# Revit family: FR_MEADRAIN_DM_Basic
name_source: partatom
category: Allgemeines Modell
revit_build: Autodesk Revit 2018 (Build: 20170223_1515(x64)
units: mm (PartAtom-declared; Revit-internal decimal feet)

## family parameters
Beim Laden mit Abzugskörper schneiden = Ja
Bemaßung runder Anschluss = Durchmesser verwenden
Gemeinsam genutzt = Nein
Kann Basisbauteil für Bewehrung sein = Nein
Raumberechnungspunkt = Nein
Teiletyp = Normal

## types (19) — shared parameters
B_Dimetre interieure_Manchon_SKUT = 150 mm  [stored 0.492126 ft]
Bauelement = Caniveau_ Eaux de surface
Beschreibung = System universel de drainage en béton polymère
Diametre exterieur du manchon_Avaloire = 122 mm  [stored 0.400262 ft]
Diametre exterieure manchon_SKUT = 160 mm  [stored 0.524934 ft]
Elément de drainage adapté pour = Les systèmes MEADRAIN DM répondent à toutes les exigences de construction de voies rapides et d'autoroutes.MEADRAIN DM est disponible en largeurs 100,150 et 200mm
Fiche technique produit = https://www.mea-group.com
Grille = Grille en fonte
Hersteller = MEA Bautechnik GmbH business unit MEA Water Management
Hersteller und Typ- Ausschreibender gleichwertig = comme MEA Bautechnik GmbH, modèle MEADRAIN DM
IfcDescription = System universel de drainage en béton polymère
IfcExportAs = IfcWasteTerminalType
IfcExportType = USERDEFINED
Lien pour les produit = https://www.mea-group.com
MEA Consignes de pose = y compris les fondations et l'enrobage
Materiaux lit/ fondations = conformément aux dessins et à la description du produits
Materiaux élément de drainage = Caniveau de drainage
Modell = MEADRAIN DM
Stirnplatte_Epaisseure = 3 mm  [stored 0.00984252 ft]
Techniques d'installation = Typ M
Typ element de drainage = Beton
Typenkommentare = Les systèmes MEADRAIN DM répondent à toutes les exigences de construction de voies rapides et d'autoroutes.MEADRAIN DM est disponible en largeurs 100,150 et 200mm
guid = cf6c1bd8-9bf4-4563-8c57-07955e2378ac
type de pente/ pourcentage de pente élement de drainage = sans pente

## per-type parameters (varying)
| type | B_Diametre interieure_Manchon_Element de revision | B_H01 | B_Hauteur_Avaloire | B_Largeur_Caniveau | Classe de charge element de drainage | Def Classe de charge_Caniveau | Diemetre exterieure manchon_Element de revision | Documents de mise en œuvre | Hauteur_Caniveau | Largeur nominal | Largeur_Caniveau | Largeur_Fondation | Longeur_Manchon_Avaloire | Longeur_Manchon_element de revision | MEA- largeur nominal | Numéro d'article_Avaloir | Numéro d'article_Caniveau | Numéro d'article_Element de revision | Numéro d'article_Grille 1 | Numéro d'article_Grille 2 | Numéro d'article_Manchon_element de revision | Numéro d'article_Plaque frontale | Numéro d'article_SKOT |
| DM 1010 | 2 mm  [stored 0.00656168 ft] | 265 mm  [stored 0.869423 ft] | 580 mm  [stored 1.90289 ft] | 154 mm  [stored 0.505249 ft] | F900 | F900 | 22 mm  [stored 0.0721785 ft] |  | 265 mm  [stored 0.869423 ft] | 100 mm  [stored 0.328084 ft] | 154 mm  [stored 0.505249 ft] | 250 mm  [stored 0.82021 ft] | 30 mm  [stored 0.0984252 ft] | 130 mm  [stored 0.426509 ft] | 1010 | 010712898 | 010712884 | 010712896 | - | 010153094 | - | 010712900 |  |
| DM 1500 | 2 mm  [stored 0.00656168 ft] | 280 mm  [stored 0.918635 ft] | 860 mm | 204 mm  [stored 0.669291 ft] | F900 | F900 | 22 mm  [stored 0.0721785 ft] |  | 280 mm  [stored 0.918635 ft] | 150 mm  [stored 0.492126 ft] | 204 mm  [stored 0.669291 ft] | 250 mm  [stored 0.82021 ft] | 194 mm  [stored 0.636483 ft] | 130 mm  [stored 0.426509 ft] | 1500 |  | 010712938 | 010712950 | 010151173 | 010151169 | - | 010712954 | 010712952 |
| DM 1540 | 140 mm  [stored 0.459318 ft] | 480 mm  [stored 1.5748 ft] | 860 mm | 204 mm  [stored 0.669291 ft] | F900 | F900 | 160 mm  [stored 0.524934 ft] |  | 480 mm  [stored 1.5748 ft] | 150 mm  [stored 0.492126 ft] | 204 mm  [stored 0.669291 ft] | 250 mm  [stored 0.82021 ft] | 194 mm  [stored 0.636483 ft] | 130 mm  [stored 0.426509 ft] | 1540 |  | 010712902 | 010712383 | 010151173 | 010151169 | 010712384 | 010712918 | 010712916 |
| DM 2000 | 180 mm  [stored 0.590551 ft] | 320 mm  [stored 1.04987 ft] | 700 mm  [stored 2.29659 ft] | 254 mm | F900 | F900 | 200 mm  [stored 0.656168 ft] |  | 320 mm  [stored 1.04987 ft] | 200 mm  [stored 0.656168 ft] | 254 mm | 250 mm  [stored 0.82021 ft] | 194 mm  [stored 0.636483 ft] | 180 mm  [stored 0.590551 ft] | 2000 |  | 010712357 | 010712386 | 010154236 | 010154237 | 010714908 | 010712375 | 010712369 |
| DM 2020 | 180 mm  [stored 0.590551 ft] | 420 mm  [stored 1.37795 ft] | 800 mm  [stored 2.62467 ft] | 254 mm | E600 | E600 | 200 mm  [stored 0.656168 ft] |  | 420 mm  [stored 1.37795 ft] | 200 mm  [stored 0.656168 ft] | 254 mm | 200 mm  [stored 0.656168 ft] | 194 mm  [stored 0.636483 ft] | 180 mm  [stored 0.590551 ft] | 2020 |  | 010712804 | 010712385 | 010154236 | 010154237 | 010714910 | 010712822 | 010712816 |
| DM 2040 | 180 mm  [stored 0.590551 ft] | 520 mm  [stored 1.70604 ft] | 950 mm  [stored 3.1168 ft] | 254 mm | E600 | E600 | 200 mm  [stored 0.656168 ft] | https://www.mea-group.com | 520 mm  [stored 1.70604 ft] | 200 mm  [stored 0.656168 ft] | 254 mm | 200 mm  [stored 0.656168 ft] | 194 mm  [stored 0.636483 ft] | 180 mm  [stored 0.590551 ft] | 2040 |  | 010712782 | 010712389 | 010154236 | 010154237 | 010714912 | 010712800 | 010712798 |
| DM 2050 | 180 mm  [stored 0.590551 ft] | 559 mm  [stored 1.83399 ft] | 950 mm  [stored 3.1168 ft] | 254 mm | E600 | E600 | 200 mm  [stored 0.656168 ft] |  | 559 mm  [stored 1.83399 ft] | 200 mm  [stored 0.656168 ft] | 254 mm | 200 mm  [stored 0.656168 ft] | 194 mm  [stored 0.636483 ft] | 180 mm  [stored 0.590551 ft] | 2050 |  | 010712762 | 010712390 | 010154236 | 010154237 | 010714914 | 010712780 | 010712778 |
| DM 1010 DAR | 2 mm  [stored 0.00656168 ft] | 265 mm  [stored 0.869423 ft] | 580 mm  [stored 1.90289 ft] | 154 mm  [stored 0.505249 ft] | F900 | F900 | 22 mm  [stored 0.0721785 ft] |  | 265 mm  [stored 0.869423 ft] | 100 mm  [stored 0.328084 ft] | 154 mm  [stored 0.505249 ft] | 250 mm  [stored 0.82021 ft] | 30 mm  [stored 0.0984252 ft] | 130 mm  [stored 0.426509 ft] | 1010 DAR | 010712892 | 010712884 | 010712896 | - | 010153094 | - | 010712900 |  |
| DM 1010 DAL | 2 mm  [stored 0.00656168 ft] | 265 mm  [stored 0.869423 ft] | 580 mm  [stored 1.90289 ft] | 154 mm  [stored 0.505249 ft] | F900 | F900 | 22 mm  [stored 0.0721785 ft] |  | 265 mm  [stored 0.869423 ft] | 100 mm  [stored 0.328084 ft] | 154 mm  [stored 0.505249 ft] | 250 mm  [stored 0.82021 ft] | 30 mm  [stored 0.0984252 ft] | 130 mm  [stored 0.426509 ft] | 1010 DAL | 010712888 | 010712884 | 010712896 | - | 010153094 | - | 010712900 |  |
| DM 1500 DAR | 2 mm  [stored 0.00656168 ft] | 280 mm  [stored 0.918635 ft] | 860 mm | 204 mm  [stored 0.669291 ft] | F900 | F900 | 22 mm  [stored 0.0721785 ft] |  | 280 mm  [stored 0.918635 ft] | 150 mm  [stored 0.492126 ft] | 204 mm  [stored 0.669291 ft] | 250 mm  [stored 0.82021 ft] | 194 mm  [stored 0.636483 ft] | 130 mm  [stored 0.426509 ft] | 1500 DAR |  | 010712956 | 010712950 | 010151173 | 010151169 | - | 010712954 | 010712952 |
| DM 1500 DAL | 2 mm  [stored 0.00656168 ft] | 280 mm  [stored 0.918635 ft] | 860 mm | 204 mm  [stored 0.669291 ft] | F900 | F900 | 22 mm  [stored 0.0721785 ft] |  | 280 mm  [stored 0.918635 ft] | 150 mm  [stored 0.492126 ft] | 204 mm  [stored 0.669291 ft] | 250 mm  [stored 0.82021 ft] | 194 mm  [stored 0.636483 ft] | 130 mm  [stored 0.426509 ft] | 1500 DAL |  | 010712938 | 010712950 | 010151173 | 010151169 | - | 010712954 | 010712952 |
| DM 1540 DAR | 140 mm  [stored 0.459318 ft] | 480 mm  [stored 1.5748 ft] | 860 mm | 204 mm  [stored 0.669291 ft] | F900 | F900 | 160 mm  [stored 0.524934 ft] |  | 480 mm  [stored 1.5748 ft] | 150 mm  [stored 0.492126 ft] | 204 mm  [stored 0.669291 ft] | 250 mm  [stored 0.82021 ft] | 194 mm  [stored 0.636483 ft] | 130 mm  [stored 0.426509 ft] | 1540 DAR |  | 010712910 | 010712383 | 010151173 | 010151169 | 010712384 | 010712918 | 010712916 |
| DM 1540 DAL | 140 mm  [stored 0.459318 ft] | 480 mm  [stored 1.5748 ft] | 860 mm | 204 mm  [stored 0.669291 ft] | F900 | F900 | 160 mm  [stored 0.524934 ft] |  | 480 mm  [stored 1.5748 ft] | 150 mm  [stored 0.492126 ft] | 204 mm  [stored 0.669291 ft] | 250 mm  [stored 0.82021 ft] | 194 mm  [stored 0.636483 ft] | 130 mm  [stored 0.426509 ft] | 1540 DAL |  | 010712906 | 010712383 | 010151173 | 010151169 | 010712384 | 010712918 | 010712916 |
| DM 2000 DAR | 180 mm  [stored 0.590551 ft] | 320 mm  [stored 1.04987 ft] | 700 mm  [stored 2.29659 ft] | 254 mm | F900 | F900 | 200 mm  [stored 0.656168 ft] |  | 320 mm  [stored 1.04987 ft] | 200 mm  [stored 0.656168 ft] | 254 mm | 250 mm  [stored 0.82021 ft] | 194 mm  [stored 0.636483 ft] | 180 mm  [stored 0.590551 ft] | 2000 DAR |  | 010712393 | 010712386 | 010154236 | 010154237 | 010714908 | 010712375 | 010712369 |
| DM 2000 DAL | 180 mm  [stored 0.590551 ft] | 320 mm  [stored 1.04987 ft] | 700 mm  [stored 2.29659 ft] | 254 mm | F900 | F900 | 200 mm  [stored 0.656168 ft] |  | 320 mm  [stored 1.04987 ft] | 200 mm  [stored 0.656168 ft] | 254 mm | 250 mm  [stored 0.82021 ft] | 194 mm  [stored 0.636483 ft] | 180 mm  [stored 0.590551 ft] | 2000 DAL |  | 010712387 | 010712386 | 010154236 | 010154237 | 010714908 | 010712375 | 010712369 |
| DM 2020 DAR | 180 mm  [stored 0.590551 ft] | 420 mm  [stored 1.37795 ft] | 800 mm  [stored 2.62467 ft] | 254 mm | E600 | E600 | 200 mm  [stored 0.656168 ft] |  | 420 mm  [stored 1.37795 ft] | 200 mm  [stored 0.656168 ft] | 254 mm | 200 mm  [stored 0.656168 ft] | 194 mm  [stored 0.636483 ft] | 180 mm  [stored 0.590551 ft] | 2020 DAR |  | 010712812 | 010712385 | 010154236 | 010154237 | 010714910 | 010712822 | 010712816 |
| DM 2020 DAL | 180 mm  [stored 0.590551 ft] | 420 mm  [stored 1.37795 ft] | 800 mm  [stored 2.62467 ft] | 254 mm | E600 | E600 | 200 mm  [stored 0.656168 ft] |  | 420 mm  [stored 1.37795 ft] | 200 mm  [stored 0.656168 ft] | 254 mm | 200 mm  [stored 0.656168 ft] | 194 mm  [stored 0.636483 ft] | 180 mm  [stored 0.590551 ft] | 2020 DAL |  | 010712808 | 010712385 | 010154236 | 010154237 | 010714910 | 010712822 | 010712816 |
| DM 2040 DAR | 180 mm  [stored 0.590551 ft] | 520 mm  [stored 1.70604 ft] | 950 mm  [stored 3.1168 ft] | 254 mm | E600 | E600 | 200 mm  [stored 0.656168 ft] |  | 520 mm  [stored 1.70604 ft] | 200 mm  [stored 0.656168 ft] | 254 mm | 200 mm  [stored 0.656168 ft] | 194 mm  [stored 0.636483 ft] | 180 mm  [stored 0.590551 ft] | 2040 DAR |  | 010712924 | 010712389 | 010154236 | 010154237 | 010714912 | 010712800 | 010712798 |
| DM 2040 DAL | 180 mm  [stored 0.590551 ft] | 520 mm  [stored 1.70604 ft] | 950 mm  [stored 3.1168 ft] | 254 mm | E600 | E600 | 200 mm  [stored 0.656168 ft] |  | 520 mm  [stored 1.70604 ft] | 200 mm  [stored 0.656168 ft] | 254 mm | 200 mm  [stored 0.656168 ft] | 194 mm  [stored 0.636483 ft] | 180 mm  [stored 0.590551 ft] | 2040 DAL |  | 010712920 | 010712389 | 010154236 | 010154237 | 010714912 | 010712800 | 010712798 |

note: [stored X ft] marks values corroborated as IEEE doubles in the binary element streams (Revit-internal decimal feet)
